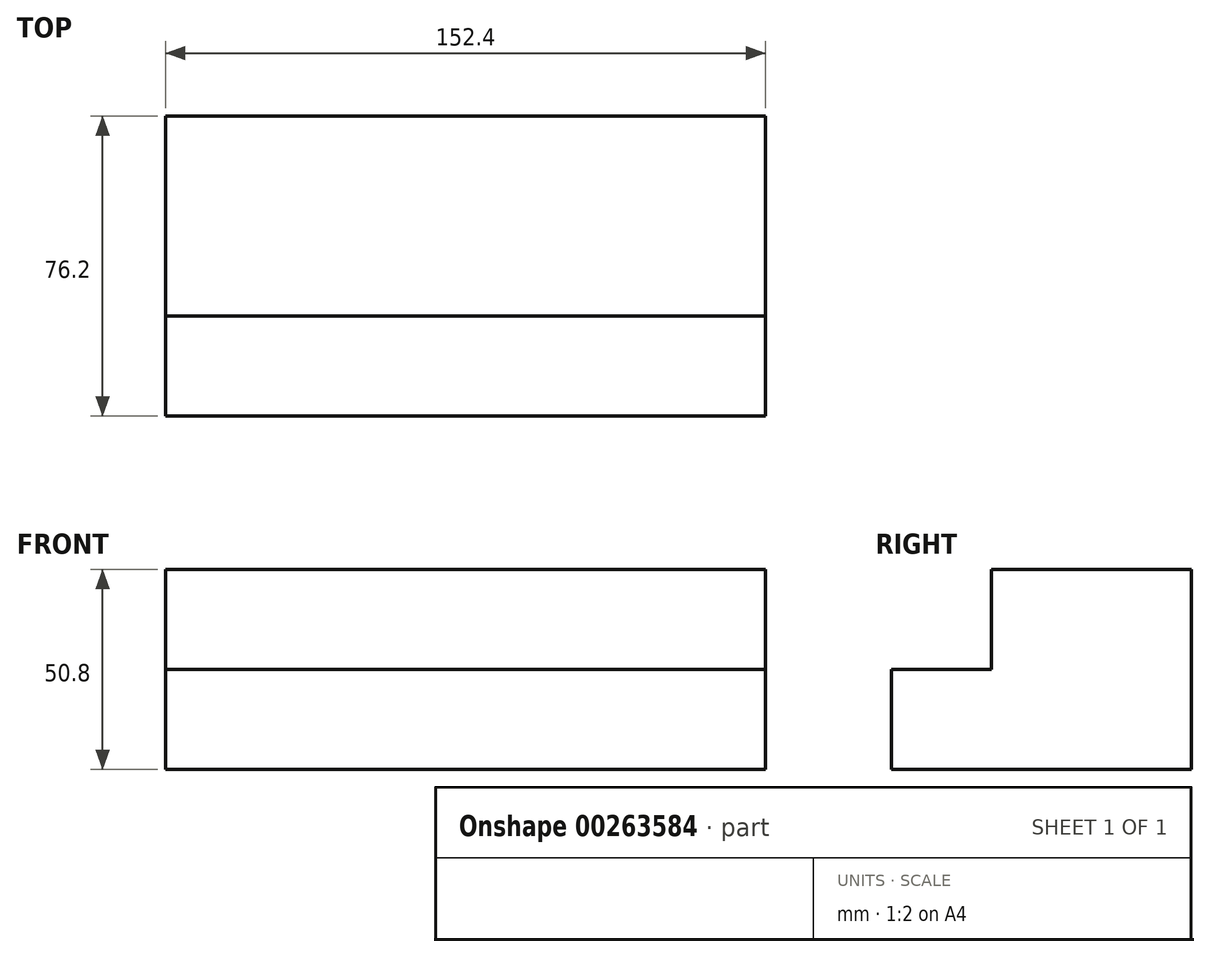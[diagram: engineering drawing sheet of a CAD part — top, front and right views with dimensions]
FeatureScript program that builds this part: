
annotation { "Feature Type Name" : "Feature", "Feature Type Description" : "" }
export const myFeature = defineFeature(function(context is Context, id is Id, definition is map)
    precondition{}
    {
        {
            var Q0;
            Q0=qCreatedBy(makeId("Front.planeOp"),FACE);
            var sketch = newSketch(context, id + "F0", { "sketchPlane" : qUnion([Q0])});
            skLineSegment(sketch, "E0.bottom", {"start": v(0, 0) * mm, "end": v(152.4, 0) * mm});
            skLineSegment(sketch, "E0.top", {"start": v(0, 25.4) * mm, "end": v(152.4, 25.4) * mm});
            skLineSegment(sketch, "E0.left", {"start": v(0, 0) * mm, "end": v(0, 25.4) * mm});
            skLineSegment(sketch, "E0.right", {"start": v(152.4, 0) * mm, "end": v(152.4, 25.4) * mm});
            skLineSegment(sketch, "E1.top", {"start": v(0, 50.8) * mm, "end": v(152.4, 50.8) * mm});
            skLineSegment(sketch, "E1.left", {"start": v(0, 25.4) * mm, "end": v(0, 50.8) * mm});
            skLineSegment(sketch, "E1.right", {"start": v(152.4, 25.4) * mm, "end": v(152.4, 50.8) * mm});
            skSolve(sketch);
        }
        {
            var Q0;
            Q0=makeQuery(id+"F0.imprint","IMPRINT",FACE,{"disambiguationData":[TD([[makeQuery(id+"F0.imprint","IMPRINT",EDGE,{"derivedFrom":sQuery(id+"F0.wireOp",EDGE,"E0.bottom")}),1.0]])]});
            extrude(context, id + "F1", {"entities" : qUnion([Q0]), "depth" : 76.2 * mm});
        }
        {
            var Q0;
            Q0=makeQuery(id+"F0.imprint","IMPRINT",FACE,{"disambiguationData":[TD([[makeQuery(id+"F0.imprint","IMPRINT",EDGE,{"derivedFrom":sQuery(id+"F0.wireOp",EDGE,"E0.top")}),1.0]])]});
            extrude(context, id + "F2", {"entities" : qUnion([Q0]), "operationType" : NewBodyOperationType.ADD, "depth" : 50.8 * mm});
        }
    });
